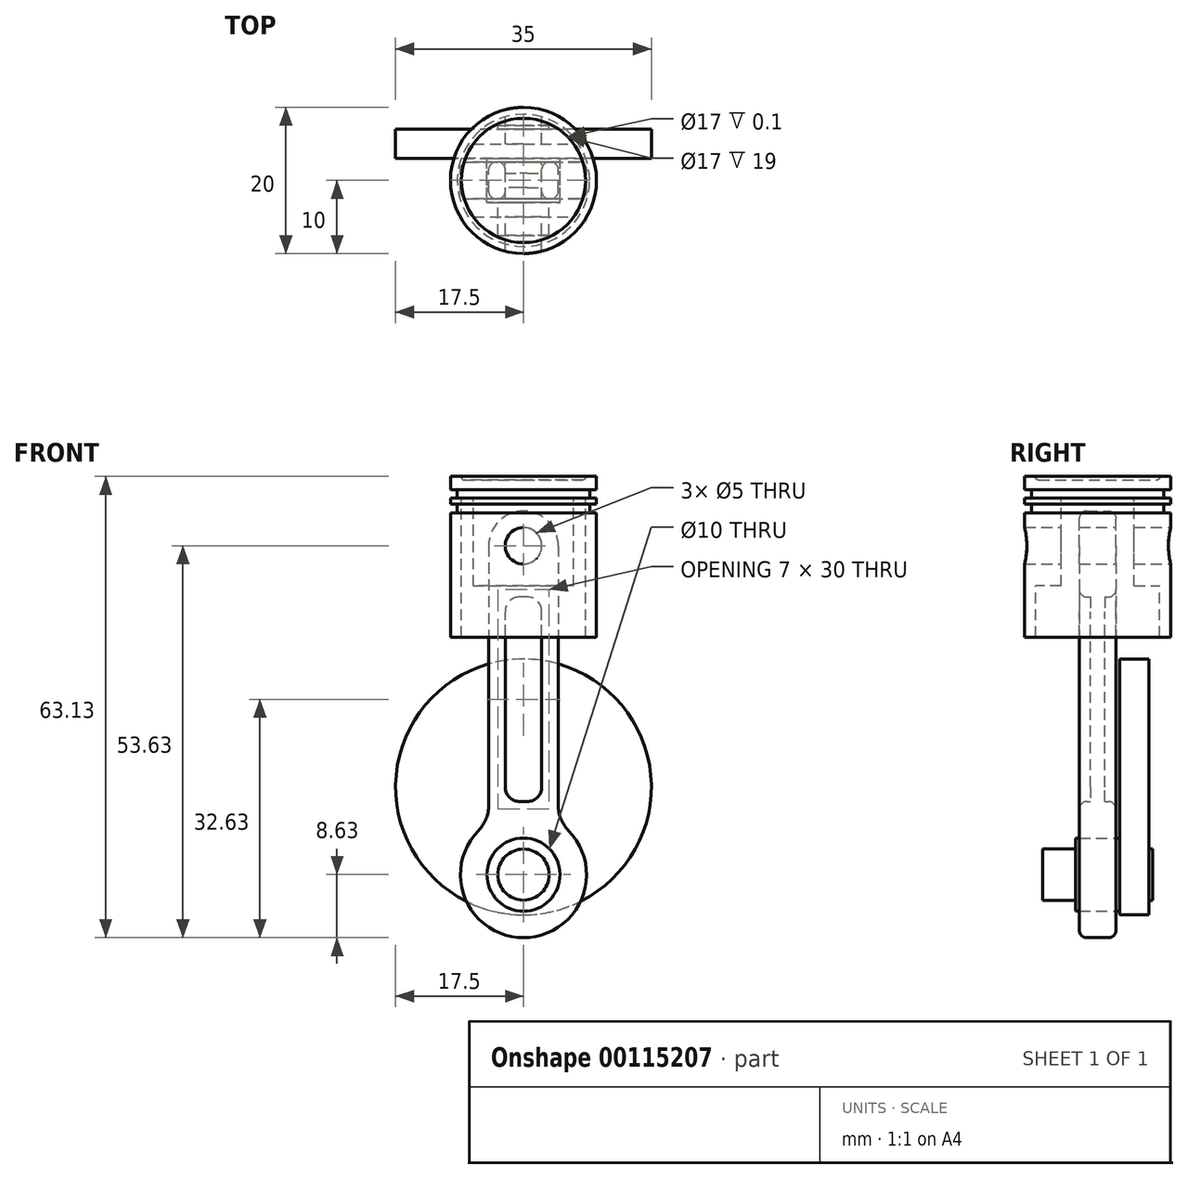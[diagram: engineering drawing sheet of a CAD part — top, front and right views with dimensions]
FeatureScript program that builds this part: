
annotation { "Feature Type Name" : "Feature", "Feature Type Description" : "" }
export const myFeature = defineFeature(function(context is Context, id is Id, definition is map)
    precondition{}
    {
        {
            var Q0;
            Q0=qCreatedBy(makeId("Front.planeOp"),FACE);
            var sketch = newSketch(context, id + "F0", { "sketchPlane" : qUnion([Q0])});
            skCircle(sketch, "E0", {"center": v(0, 0) * mm, "radius": 17.5 * mm});
            skLineSegment(sketch, "E1.bottom", {"start": v(10, 42.5) * mm, "end": v(-10, 42.5) * mm});
            skLineSegment(sketch, "E1.top", {"start": v(10, 27.5) * mm, "end": v(-10, 27.5) * mm});
            skLineSegment(sketch, "E1.left", {"start": v(10, 42.5) * mm, "end": v(10, 27.5) * mm});
            skLineSegment(sketch, "E1.right", {"start": v(-10, 42.5) * mm, "end": v(-10, 27.5) * mm});
            skPoint(sketch, "E1.middle", {"position": v(0, 35) * mm});
            skCircle(sketch, "E2", {"center": v(0, -12) * mm, "radius": 3.5 * mm});
            skCircle(sketch, "E3", {"center": v(0, 33) * mm, "radius": 2.5 * mm});
            skLineSegment(sketch, "E4.bottom", {"start": v(-10, 40.7) * mm, "end": v(-9.05, 40.7) * mm});
            skLineSegment(sketch, "E4.top", {"start": v(-10, 39.5) * mm, "end": v(-9.05, 39.5) * mm});
            skLineSegment(sketch, "E4.left", {"start": v(-10, 40.7) * mm, "end": v(-10, 39.5) * mm});
            skLineSegment(sketch, "E4.right", {"start": v(-9.05, 40.7) * mm, "end": v(-9.05, 39.5) * mm});
            skLineSegment(sketch, "E5.bottom", {"start": v(-10, 38.7) * mm, "end": v(-9.05, 38.7) * mm});
            skLineSegment(sketch, "E5.top", {"start": v(-10, 37.5) * mm, "end": v(-9.05, 37.5) * mm});
            skLineSegment(sketch, "E5.left", {"start": v(-10, 38.7) * mm, "end": v(-10, 37.5) * mm});
            skLineSegment(sketch, "E5.right", {"start": v(-9.05, 38.7) * mm, "end": v(-9.05, 37.5) * mm});
            skLineSegment(sketch, "E6", {"start": v(0, 33) * mm, "end": v(0, 21.27) * mm, "construction": true});
            skPoint(sketch, "E6.endSnap0", {"position": v(0, 27.5) * mm});
            skSolve(sketch);
        }
        {
            var Q0;
            Q0=qCreatedBy(makeId("Front.planeOp"),FACE);
            var sketch = newSketch(context, id + "F1", { "sketchPlane" : qUnion([Q0])});
            skCircle(sketch, "E7", {"center": v(0, -12) * mm, "radius": 5 * mm});
            skCircle(sketch, "E8", {"center": v(0, 33) * mm, "radius": 2.5 * mm});
            skArc(sketch, "E9", {"start": v(-4.76, -4.8) * mm, "mid": v(0, -20.63) * mm, "end": v(4.76, -4.8) * mm});
            skArc(sketch, "E10", {"start": v(4.76, 33) * mm, "mid": v(0, 37.76) * mm, "end": v(-4.76, 33) * mm});
            skLineSegment(sketch, "E11", {"start": v(-4.76, 33) * mm, "end": v(-4.76, -4.8) * mm});
            skLineSegment(sketch, "E12", {"start": v(4.76, 33) * mm, "end": v(4.76, -4.8) * mm});
            skLineSegment(sketch, "E13.bottom", {"start": v(2.5, -2) * mm, "end": v(-2.5, -2) * mm});
            skLineSegment(sketch, "E13.top", {"start": v(2.5, 26) * mm, "end": v(-2.5, 26) * mm});
            skLineSegment(sketch, "E13.left", {"start": v(2.5, -2) * mm, "end": v(2.5, 26) * mm});
            skLineSegment(sketch, "E13.right", {"start": v(-2.5, -2) * mm, "end": v(-2.5, 26) * mm});
            skPoint(sketch, "E13.middle", {"position": v(0, 12) * mm});
            skSolve(sketch);
        }
        {
            var Q0;
            Q0=sQuery(id+"F0.wireOp",EDGE,"E1.bottom");
            cPlane(context, id + "F2", {"entities" : qUnion([Q0]), "cplaneType" : CPlaneType.LINE_ANGLE, "offset" : 25 * mm, "angle" : 90 * degree, "width" : 150 * mm, "height" : 150 * mm});
        }
        {
            var Q0;
            Q0=qCreatedBy(id+"F2.planeOp",FACE);
            var sketch = newSketch(context, id + "F3", { "sketchPlane" : qUnion([Q0])});
            skCircle(sketch, "E14", {"center": v(0, 0) * mm, "radius": 10 * mm});
            skCircle(sketch, "E15", {"center": v(0, 0) * mm, "radius": 8.5 * mm});
            skLineSegment(sketch, "E16", {"start": v(-6.87, 5) * mm, "end": v(6.87, 5) * mm});
            skLineSegment(sketch, "E17", {"start": v(-6.87, -5) * mm, "end": v(6.87, -5) * mm});
            skSolve(sketch);
        }
        {
            var Q0;
            Q0=makeQuery(id+"F1.imprint","IMPRINT",FACE,{"disambiguationData":[TD([[makeQuery(id+"F1.imprint","IMPRINT",EDGE,{"derivedFrom":sQuery(id+"F1.wireOp",EDGE,"E7")}),-1.0]])]});
            extrude(context, id + "F4", {"entities" : qUnion([Q0]), "endBound" : BoundingType.SYMMETRIC, "depth" : 5 * mm});
        }
        {
            var Q0;
            Q0=makeQuery(id+"F1.imprint","IMPRINT",FACE,{"disambiguationData":[TD([[makeQuery(id+"F1.imprint","IMPRINT",EDGE,{"derivedFrom":sQuery(id+"F1.wireOp",EDGE,"E13.bottom")}),-1.0]])]});
            extrude(context, id + "F5", {"entities" : qUnion([Q0]), "operationType" : NewBodyOperationType.ADD, "endBound" : BoundingType.SYMMETRIC, "depth" : 2 * mm});
        }
        {
            var Q0;
            Q0=makeQuery(id+"F4.opExtrude","SWEPT_EDGE",EDGE,{"disambiguationData":[OSD([sQuery(id+"F1.wireOp",EDGE,"E9"),sQuery(id+"F1.wireOp",EDGE,"E12")])]});
            var Q1;
            Q1=makeQuery(id+"F4.opExtrude","SWEPT_EDGE",EDGE,{"disambiguationData":[OSD([sQuery(id+"F1.wireOp",EDGE,"E9"),sQuery(id+"F1.wireOp",EDGE,"E11")])]});
            fillet(context, id + "F6", {"entities" : qUnion([Q0, Q1]), "radius" : 5 * mm, "tangentPropagation" : true, "allowEdgeOverflow" : false});
        }
        {
            var Q0;
            {var subQ0=sQuery(id+"F1.wireOp",EDGE,"E13.right");var subQ1=sQuery(id+"F1.wireOp",EDGE,"E13.left");var subQ2=sQuery(id+"F1.wireOp",EDGE,"E13.top");var subQ3=sQuery(id+"F1.wireOp",EDGE,"E13.bottom");Q0=makeQuery(id+"F5.boolean.opBoolean","SPLIT",EDGE,{"disambiguationData":[TD([makeQuery(id+"F5.opExtrude","CAP_FACE",FACE,{"disambiguationData":[OSD([subQ3,subQ2,subQ1,subQ0])],"isStart":false})])],"derivedFrom":makeQuery(id+"F4.opExtrude","SWEPT_EDGE",EDGE,{"disambiguationData":[OSD([subQ3,subQ1])]})});}
            var Q1;
            {var subQ0=sQuery(id+"F1.wireOp",EDGE,"E13.right");var subQ1=sQuery(id+"F1.wireOp",EDGE,"E13.left");var subQ2=sQuery(id+"F1.wireOp",EDGE,"E13.top");var subQ3=sQuery(id+"F1.wireOp",EDGE,"E13.bottom");Q1=makeQuery(id+"F5.boolean.opBoolean","SPLIT",EDGE,{"disambiguationData":[TD([makeQuery(id+"F5.opExtrude","CAP_FACE",FACE,{"disambiguationData":[OSD([subQ3,subQ2,subQ1,subQ0])],"isStart":false})])],"derivedFrom":makeQuery(id+"F4.opExtrude","SWEPT_EDGE",EDGE,{"disambiguationData":[OSD([subQ3,subQ0])]})});}
            var Q2;
            {var subQ0=sQuery(id+"F1.wireOp",EDGE,"E13.right");var subQ1=sQuery(id+"F1.wireOp",EDGE,"E13.left");var subQ2=sQuery(id+"F1.wireOp",EDGE,"E13.top");var subQ3=sQuery(id+"F1.wireOp",EDGE,"E13.bottom");Q2=makeQuery(id+"F5.boolean.opBoolean","SPLIT",EDGE,{"disambiguationData":[TD([makeQuery(id+"F5.opExtrude","CAP_FACE",FACE,{"disambiguationData":[OSD([subQ3,subQ2,subQ1,subQ0])],"isStart":false})])],"derivedFrom":makeQuery(id+"F4.opExtrude","SWEPT_EDGE",EDGE,{"disambiguationData":[OSD([subQ2,subQ1])]})});}
            var Q3;
            {var subQ0=sQuery(id+"F1.wireOp",EDGE,"E13.right");var subQ1=sQuery(id+"F1.wireOp",EDGE,"E13.left");var subQ2=sQuery(id+"F1.wireOp",EDGE,"E13.top");var subQ3=sQuery(id+"F1.wireOp",EDGE,"E13.bottom");Q3=makeQuery(id+"F5.boolean.opBoolean","SPLIT",EDGE,{"disambiguationData":[TD([makeQuery(id+"F5.opExtrude","CAP_FACE",FACE,{"disambiguationData":[OSD([subQ3,subQ2,subQ1,subQ0])],"isStart":false})])],"derivedFrom":makeQuery(id+"F4.opExtrude","SWEPT_EDGE",EDGE,{"disambiguationData":[OSD([subQ2,subQ0])]})});}
            var Q4;
            {var subQ0=sQuery(id+"F1.wireOp",EDGE,"E13.right");var subQ1=sQuery(id+"F1.wireOp",EDGE,"E13.left");var subQ2=sQuery(id+"F1.wireOp",EDGE,"E13.top");var subQ3=sQuery(id+"F1.wireOp",EDGE,"E13.bottom");Q4=makeQuery(id+"F5.boolean.opBoolean","SPLIT",EDGE,{"disambiguationData":[TD([makeQuery(id+"F5.opExtrude","CAP_FACE",FACE,{"disambiguationData":[OSD([subQ3,subQ2,subQ1,subQ0])],"isStart":true})])],"derivedFrom":makeQuery(id+"F4.opExtrude","SWEPT_EDGE",EDGE,{"disambiguationData":[OSD([subQ2,subQ0])]})});}
            var Q5;
            {var subQ0=sQuery(id+"F1.wireOp",EDGE,"E13.right");var subQ1=sQuery(id+"F1.wireOp",EDGE,"E13.left");var subQ2=sQuery(id+"F1.wireOp",EDGE,"E13.top");var subQ3=sQuery(id+"F1.wireOp",EDGE,"E13.bottom");Q5=makeQuery(id+"F5.boolean.opBoolean","SPLIT",EDGE,{"disambiguationData":[TD([makeQuery(id+"F5.opExtrude","CAP_FACE",FACE,{"disambiguationData":[OSD([subQ3,subQ2,subQ1,subQ0])],"isStart":true})])],"derivedFrom":makeQuery(id+"F4.opExtrude","SWEPT_EDGE",EDGE,{"disambiguationData":[OSD([subQ2,subQ1])]})});}
            var Q6;
            {var subQ0=sQuery(id+"F1.wireOp",EDGE,"E13.right");var subQ1=sQuery(id+"F1.wireOp",EDGE,"E13.left");var subQ2=sQuery(id+"F1.wireOp",EDGE,"E13.top");var subQ3=sQuery(id+"F1.wireOp",EDGE,"E13.bottom");Q6=makeQuery(id+"F5.boolean.opBoolean","SPLIT",EDGE,{"disambiguationData":[TD([makeQuery(id+"F5.opExtrude","CAP_FACE",FACE,{"disambiguationData":[OSD([subQ3,subQ2,subQ1,subQ0])],"isStart":true})])],"derivedFrom":makeQuery(id+"F4.opExtrude","SWEPT_EDGE",EDGE,{"disambiguationData":[OSD([subQ3,subQ0])]})});}
            var Q7;
            {var subQ0=sQuery(id+"F1.wireOp",EDGE,"E13.right");var subQ1=sQuery(id+"F1.wireOp",EDGE,"E13.left");var subQ2=sQuery(id+"F1.wireOp",EDGE,"E13.top");var subQ3=sQuery(id+"F1.wireOp",EDGE,"E13.bottom");Q7=makeQuery(id+"F5.boolean.opBoolean","SPLIT",EDGE,{"disambiguationData":[TD([makeQuery(id+"F5.opExtrude","CAP_FACE",FACE,{"disambiguationData":[OSD([subQ3,subQ2,subQ1,subQ0])],"isStart":true})])],"derivedFrom":makeQuery(id+"F4.opExtrude","SWEPT_EDGE",EDGE,{"disambiguationData":[OSD([subQ3,subQ1])]})});}
            fillet(context, id + "F7", {"entities" : qUnion([Q0, Q1, Q2, Q3, Q4, Q5, Q6, Q7]), "radius" : 2 * mm, "tangentPropagation" : true, "allowEdgeOverflow" : false});
        }
        {
            var Q0;
            Q0=makeQuery(id+"F4.opExtrude","CAP_EDGE",EDGE,{"disambiguationData":[OSD([sQuery(id+"F1.wireOp",EDGE,"E12")])],"isStart":true});
            var Q1;
            Q1=makeQuery(id+"F4.opExtrude","CAP_EDGE",EDGE,{"disambiguationData":[OSD([sQuery(id+"F1.wireOp",EDGE,"E11")])],"isStart":false});
            var Q2;
            {var subQ0=sQuery(id+"F1.wireOp",EDGE,"E13.right");var subQ1=sQuery(id+"F1.wireOp",EDGE,"E13.left");var subQ2=sQuery(id+"F1.wireOp",EDGE,"E13.top");var subQ3=sQuery(id+"F1.wireOp",EDGE,"E13.bottom");var subQ4=makeQuery(id+"F4.opExtrude","CAP_FACE",FACE,{"disambiguationData":[OSD([sQuery(id+"F1.wireOp",EDGE,"E7"),sQuery(id+"F1.wireOp",EDGE,"E8"),sQuery(id+"F1.wireOp",EDGE,"E9"),sQuery(id+"F1.wireOp",EDGE,"E10"),sQuery(id+"F1.wireOp",EDGE,"E11"),sQuery(id+"F1.wireOp",EDGE,"E12"),subQ3,subQ2,subQ1,subQ0])],"isStart":true});Q2=makeQuery(id+"F7.opFillet","BLEND_EDGE",EDGE,{"blendedFrom":[makeQuery(id+"F5.boolean.opBoolean","SPLIT",EDGE,{"disambiguationData":[TD([makeQuery(id+"F5.opExtrude","CAP_FACE",FACE,{"disambiguationData":[OSD([subQ3,subQ2,subQ1,subQ0])],"isStart":true})])],"derivedFrom":makeQuery(id+"F4.opExtrude","SWEPT_EDGE",EDGE,{"disambiguationData":[OSD([subQ2,subQ0])]})}),subQ4],"blendedInto":[subQ4]});}
            var Q3;
            Q3=makeQuery(id+"F4.opExtrude","CAP_EDGE",EDGE,{"disambiguationData":[OSD([sQuery(id+"F1.wireOp",EDGE,"E13.right")])],"isStart":false});
            fillet(context, id + "F8", {"entities" : qUnion([Q0, Q1, Q2, Q3]), "radius" : 1 * mm, "tangentPropagation" : true, "allowEdgeOverflow" : false});
        }
        {
            var Q0;
            Q0=makeQuery(id+"F0.imprint","IMPRINT",FACE,{"disambiguationData":[TD([[makeQuery(id+"F0.imprint","IMPRINT",EDGE,{"derivedFrom":sQuery(id+"F0.wireOp",EDGE,"E0")}),1.0]])]});
            var Q1;
            Q1=makeQuery(id+"F4.opExtrude","CAP_FACE",FACE,{"disambiguationData":[OSD([sQuery(id+"F1.wireOp",EDGE,"E7"),sQuery(id+"F1.wireOp",EDGE,"E8"),sQuery(id+"F1.wireOp",EDGE,"E9"),sQuery(id+"F1.wireOp",EDGE,"E10"),sQuery(id+"F1.wireOp",EDGE,"E11"),sQuery(id+"F1.wireOp",EDGE,"E12"),sQuery(id+"F1.wireOp",EDGE,"E13.bottom"),sQuery(id+"F1.wireOp",EDGE,"E13.top"),sQuery(id+"F1.wireOp",EDGE,"E13.left"),sQuery(id+"F1.wireOp",EDGE,"E13.right")])],"isStart":true});
            extrude(context, id + "F9", {"entities" : qUnion([Q0]), "oppositeDirection" : true, "endBoundEntityFace" : qUnion([Q1]), "depth" : 7 * mm, "hasSecondDirection" : true, "secondDirectionOppositeDirection" : true, "secondDirectionDepth" : 3 * mm});
        }
        {
            var Q0;
            Q0=makeQuery(id+"F1.imprint","IMPRINT",FACE,{"disambiguationData":[TD([[makeQuery(id+"F1.imprint","IMPRINT",EDGE,{"derivedFrom":sQuery(id+"F1.wireOp",EDGE,"E7")}),1.0]])]});
            extrude(context, id + "F10", {"entities" : qUnion([Q0]), "endBound" : BoundingType.SYMMETRIC, "depth" : 6 * mm});
        }
        {
            var Q0;
            Q0=qCreatedBy(makeId("Front.planeOp"),FACE);
            var sketch = newSketch(context, id + "F11", { "sketchPlane" : qUnion([Q0])});
            skCircle(sketch, "E18.0", {"center": v(0, -12) * mm, "radius": 3.5 * mm});
            skSolve(sketch);
        }
        {
            var Q0;
            Q0 = qSketchRegion(id + "F11", true);
            extrude(context, id + "F12", {"entities" : qUnion([Q0]), "operationType" : NewBodyOperationType.ADD, "endBound" : BoundingType.SYMMETRIC, "depth" : 15 * mm});
        }
        {
            var Q0;
            Q0=makeQuery(id+"F3.imprint","IMPRINT",FACE,{"disambiguationData":[TD([[makeQuery(id+"F3.imprint","IMPRINT",EDGE,{"derivedFrom":sQuery(id+"F3.wireOp",EDGE,"E14")}),1.0]])]});
            extrude(context, id + "F13", {"entities" : qUnion([Q0]), "oppositeDirection" : true, "depth" : 22 * mm});
        }
        {
            var Q0;
            {var subQ0=sQuery(id+"F3.wireOp",EDGE,"E16");Q0=makeQuery(id+"F3.imprint","IMPRINT",FACE,{"disambiguationData":[TD([[makeQuery(id+"F3.imprint","IMPRINT",EDGE,{"derivedFrom":subQ0}),1.0]])]});}
            var Q1;
            {var subQ0=sQuery(id+"F3.wireOp",EDGE,"E17");Q1=makeQuery(id+"F3.imprint","IMPRINT",FACE,{"disambiguationData":[TD([[makeQuery(id+"F3.imprint","IMPRINT",EDGE,{"derivedFrom":subQ0}),-1.0]])]});}
            extrude(context, id + "F14", {"entities" : qUnion([Q0, Q1]), "operationType" : NewBodyOperationType.ADD, "oppositeDirection" : true, "depth" : 15 * mm});
        }
        {
            var Q0;
            {var subQ0=sQuery(id+"F3.wireOp",EDGE,"E16");Q0=makeQuery(id+"F3.imprint","IMPRINT",FACE,{"disambiguationData":[TD([[makeQuery(id+"F3.imprint","IMPRINT",EDGE,{"derivedFrom":subQ0}),-1.0]])]});}
            extrude(context, id + "F15", {"entities" : qUnion([Q0]), "operationType" : NewBodyOperationType.ADD, "oppositeDirection" : true, "depth" : 3 * mm});
        }
        {
            var Q0;
            Q0=makeQuery(id+"F0.imprint","IMPRINT",FACE,{"disambiguationData":[TD([[makeQuery(id+"F0.imprint","IMPRINT",EDGE,{"derivedFrom":sQuery(id+"F0.wireOp",EDGE,"E3")}),1.0]])]});
            extrude(context, id + "F16", {"entities" : qUnion([Q0]), "operationType" : NewBodyOperationType.REMOVE, "endBound" : BoundingType.SYMMETRIC, "depth" : 22 * mm});
        }
        {
            var Q0;
            {var subQ0=sQuery(id+"F3.wireOp",EDGE,"E17");Q0=makeQuery(id+"F3.imprint","IMPRINT",FACE,{"disambiguationData":[TD([[makeQuery(id+"F3.imprint","IMPRINT",EDGE,{"derivedFrom":subQ0}),-1.0]])]});}
            var Q1;
            {var subQ0=sQuery(id+"F3.wireOp",EDGE,"E16");Q1=makeQuery(id+"F3.imprint","IMPRINT",FACE,{"disambiguationData":[TD([[makeQuery(id+"F3.imprint","IMPRINT",EDGE,{"derivedFrom":subQ0}),-1.0]])]});}
            var Q2;
            {var subQ0=sQuery(id+"F3.wireOp",EDGE,"E16");Q2=makeQuery(id+"F3.imprint","IMPRINT",FACE,{"disambiguationData":[TD([[makeQuery(id+"F3.imprint","IMPRINT",EDGE,{"derivedFrom":subQ0}),1.0]])]});}
            extrude(context, id + "F17", {"entities" : qUnion([Q0, Q1, Q2]), "operationType" : NewBodyOperationType.REMOVE, "oppositeDirection" : true, "depth" : 0.5 * mm});
        }
        {
            var Q0;
            Q0=makeQuery(id+"F0.imprint","IMPRINT",FACE,{"disambiguationData":[TD([[makeQuery(id+"F0.imprint","IMPRINT",EDGE,{"derivedFrom":sQuery(id+"F0.wireOp",EDGE,"E5.bottom")}),-1.0]])]});
            var Q1;
            Q1=makeQuery(id+"F0.imprint","IMPRINT",FACE,{"disambiguationData":[TD([[makeQuery(id+"F0.imprint","IMPRINT",EDGE,{"derivedFrom":sQuery(id+"F0.wireOp",EDGE,"E4.bottom")}),-1.0]])]});
            var Q2;
            Q2=sQuery(id+"F0.wireOp",EDGE,"E6");
            revolve(context, id + "F18", {"operationType" : NewBodyOperationType.REMOVE, "entities" : qUnion([Q0, Q1]), "axis" : qUnion([Q2]), "revolveType" : RevolveType.FULL});
        }
        {
            var Q0;
            Q0=makeQuery(id+"F17.boolean.opBoolean","COPY",EDGE,{"derivedFrom":makeQuery(id+"F17.opExtrude","CAP_EDGE",EDGE,{"disambiguationData":[OSD([sQuery(id+"F3.wireOp",EDGE,"E15")])],"isStart":false})});
            fillet(context, id + "F19", {"entities" : qUnion([Q0]), "radius" : 0.4 * mm, "tangentPropagation" : true, "allowEdgeOverflow" : false});
        }
    });
